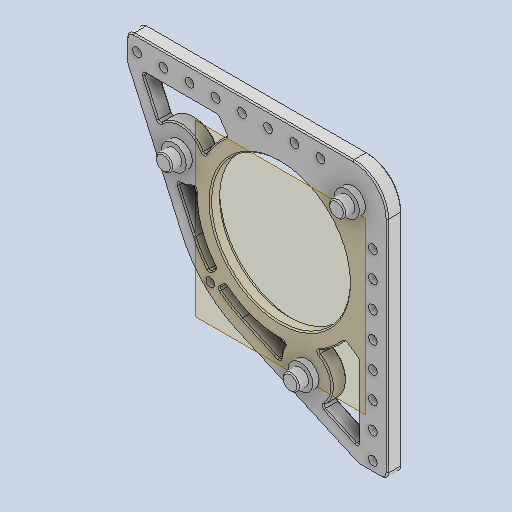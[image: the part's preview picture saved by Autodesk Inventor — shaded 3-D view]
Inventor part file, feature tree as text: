
AUTODESK INVENTOR PART (.ipt)
format: ipt  version: 2022 (Build 260153000, 153)  size: 402,944 bytes
history: native  units: in
note: dims shown in document units (in); Inventor stores cm internally (conversion verified against a paired STEP export)
features: sketch x4, other x3, plane x1
ambient origin geometry x8: Origin, YZ Plane, XZ Plane, XY Plane, X Axis, Y Axis, Z Axis, Center Point
bodies: Solid1 (feature_tree)
feature tree (8):
  other  "lower_plate.ipt"
  other  "Solid1::lower_plate.ipt"
  other  "TaggingFeature1"
  sketch  "Sketch1"  dims[d0=0.3937in]
  sketch  "Sketch4"
  sketch  "Sketch5"
  sketch  "Sketch6"
  plane  "Work Plane1"
